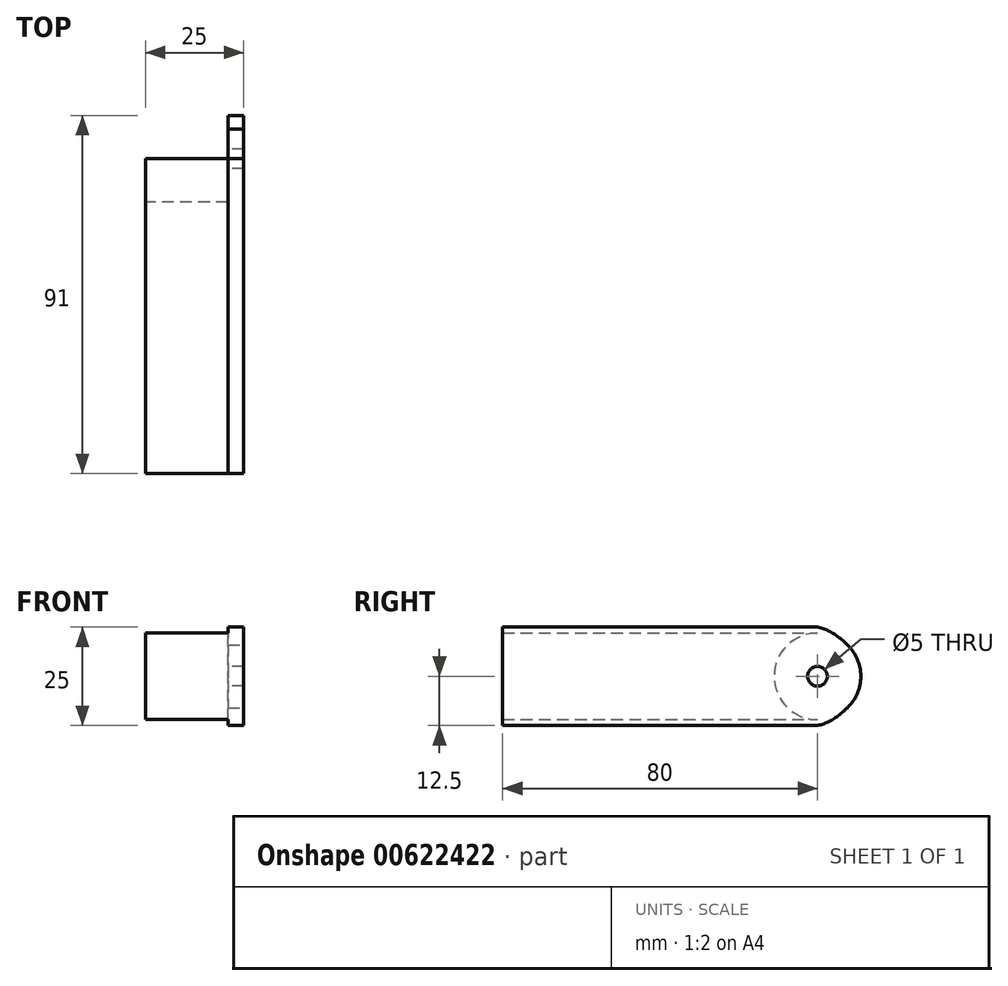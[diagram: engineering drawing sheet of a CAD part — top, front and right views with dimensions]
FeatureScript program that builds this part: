
annotation { "Feature Type Name" : "Feature", "Feature Type Description" : "" }
export const myFeature = defineFeature(function(context is Context, id is Id, definition is map)
    precondition{}
    {
        {
            var Q0;
            Q0=qCreatedBy(makeId("Front.planeOp"),FACE);
            var sketch = newSketch(context, id + "F0", { "sketchPlane" : qUnion([Q0])});
            skLineSegment(sketch, "E0.bottom", {"start": v(12.5, -12.5) * mm, "end": v(-12.5, -12.5) * mm});
            skLineSegment(sketch, "E0.top", {"start": v(12.5, 12.5) * mm, "end": v(-12.5, 12.5) * mm});
            skLineSegment(sketch, "E0.left", {"start": v(12.5, -12.5) * mm, "end": v(12.5, 12.5) * mm});
            skLineSegment(sketch, "E0.right", {"start": v(-12.5, -12.5) * mm, "end": v(-12.5, 12.5) * mm});
            skPoint(sketch, "E0.middle", {"position": v(0, 0) * mm});
            skSolve(sketch);
        }
        {
            var Q0;
            Q0 = qSketchRegion(id + "F0", true);
            extrude(context, id + "F1", {"entities" : qUnion([Q0]), "endBound" : BoundingType.SYMMETRIC, "depth" : 80 * mm, "offsetDistance" : 25 * mm});
        }
        {
            var Q0;
            Q0=makeQuery(id+"F1.opExtrude","SWEPT_FACE",FACE,{"disambiguationData":[OSD([sQuery(id+"F0.wireOp",EDGE,"E0.top")])]});
            var sketch = newSketch(context, id + "F2", { "sketchPlane" : qUnion([Q0])});
            skLineSegment(sketch, "E1.bottom", {"start": v(-12.5, 40) * mm, "end": v(8.5, 40) * mm});
            skLineSegment(sketch, "E1.top", {"start": v(-12.5, -40) * mm, "end": v(8.5, -40) * mm});
            skLineSegment(sketch, "E1.left", {"start": v(-12.5, 40) * mm, "end": v(-12.5, -40) * mm});
            skLineSegment(sketch, "E1.right", {"start": v(8.5, 40) * mm, "end": v(8.5, -40) * mm});
            skSolve(sketch);
        }
        {
            var Q0;
            Q0 = qSketchRegion(id + "F2", true);
            extrude(context, id + "F3", {"entities" : qUnion([Q0]), "operationType" : NewBodyOperationType.REMOVE, "oppositeDirection" : true, "depth" : 1.5 * mm, "offsetDistance" : 25 * mm});
        }
        {
            var Q0;
            Q0=makeQuery(id+"F1.opExtrude","SWEPT_FACE",FACE,{"disambiguationData":[OSD([sQuery(id+"F0.wireOp",EDGE,"E0.bottom")])]});
            var sketch = newSketch(context, id + "F4", { "sketchPlane" : qUnion([Q0])});
            skLineSegment(sketch, "E2.bottom", {"start": v(-12.5, 40) * mm, "end": v(8.5, 40) * mm});
            skLineSegment(sketch, "E2.top", {"start": v(-12.5, -40) * mm, "end": v(8.5, -40) * mm});
            skLineSegment(sketch, "E2.left", {"start": v(-12.5, 40) * mm, "end": v(-12.5, -40) * mm});
            skLineSegment(sketch, "E2.right", {"start": v(8.5, 40) * mm, "end": v(8.5, -40) * mm});
            skSolve(sketch);
        }
        {
            var Q0;
            Q0 = qSketchRegion(id + "F4", true);
            extrude(context, id + "F5", {"entities" : qUnion([Q0]), "operationType" : NewBodyOperationType.REMOVE, "oppositeDirection" : true, "depth" : 1.5 * mm, "offsetDistance" : 25 * mm});
        }
        {
            var Q0;
            Q0=makeQuery(id+"F1.opExtrude","SWEPT_FACE",FACE,{"disambiguationData":[OSD([sQuery(id+"F0.wireOp",EDGE,"E0.right")])]});
            var sketch = newSketch(context, id + "F6", { "sketchPlane" : qUnion([Q0])});
            skArc(sketch, "E3", {"start": v(-40, -11) * mm, "mid": v(-29, 0) * mm, "end": v(-40, 11) * mm});
            skLineSegment(sketch, "E4", {"start": v(-40, 11) * mm, "end": v(-40, -11) * mm});
            skSolve(sketch);
        }
        {
            var Q0;
            Q0 = qSketchRegion(id + "F6", true);
            extrude(context, id + "F7", {"entities" : qUnion([Q0]), "operationType" : NewBodyOperationType.REMOVE, "oppositeDirection" : true, "depth" : 21 * mm, "offsetDistance" : 25 * mm});
        }
        {
            var Q0;
            Q0=makeQuery(id+"F7.boolean.opBoolean","COPY",FACE,{"derivedFrom":makeQuery(id+"F7.opExtrude","CAP_FACE",FACE,{"disambiguationData":[OSD([sQuery(id+"F6.wireOp",EDGE,"E3"),sQuery(id+"F6.wireOp",EDGE,"E4")])],"isStart":false})});
            var sketch = newSketch(context, id + "F8", { "sketchPlane" : qUnion([Q0])});
            skLineSegment(sketch, "E5", {"start": v(-40, 11) * mm, "end": v(-40, -11) * mm});
            skArc(sketch, "E6", {"start": v(-40, 11) * mm, "mid": v(-51, 0) * mm, "end": v(-40, -11) * mm});
            skSolve(sketch);
        }
        {
            var Q0;
            Q0 = qSketchRegion(id + "F8", true);
            extrude(context, id + "F9", {"entities" : qUnion([Q0]), "operationType" : NewBodyOperationType.ADD, "oppositeDirection" : true, "depth" : 4 * mm, "offsetDistance" : 25 * mm});
        }
        {
            var Q0;
            Q0=makeQuery(id+"F9.boolean.opBoolean","MERGE",FACE,{"derivedFrom":[makeQuery(id+"F7.boolean.opBoolean","COPY",FACE,{"derivedFrom":makeQuery(id+"F7.opExtrude","CAP_FACE",FACE,{"disambiguationData":[OSD([sQuery(id+"F6.wireOp",EDGE,"E3"),sQuery(id+"F6.wireOp",EDGE,"E4")])],"isStart":false})}),makeQuery(id+"F9.opExtrude","CAP_FACE",FACE,{"disambiguationData":[OSD([sQuery(id+"F8.wireOp",EDGE,"E5"),sQuery(id+"F8.wireOp",EDGE,"E6")])],"isStart":true})]});
            var sketch = newSketch(context, id + "F10", { "sketchPlane" : qUnion([Q0])});
            skCircle(sketch, "E7", {"center": v(-40, 0) * mm, "radius": 2.5 * mm});
            skSolve(sketch);
        }
        {
            var Q0;
            Q0 = qSketchRegion(id + "F10", true);
            extrude(context, id + "F11", {"entities" : qUnion([Q0]), "operationType" : NewBodyOperationType.REMOVE, "endBound" : BoundingType.THROUGH_ALL, "oppositeDirection" : true, "depth" : 25 * mm, "offsetDistance" : 25 * mm});
        }
        {
            var Q0;
            Q0=makeQuery(id+"F9.boolean.opBoolean","MERGE",FACE,{"derivedFrom":[makeQuery(id+"F1.opExtrude","SWEPT_FACE",FACE,{"disambiguationData":[OSD([sQuery(id+"F0.wireOp",EDGE,"E0.left")])]}),makeQuery(id+"F9.opExtrude","CAP_FACE",FACE,{"disambiguationData":[OSD([sQuery(id+"F8.wireOp",EDGE,"E5"),sQuery(id+"F8.wireOp",EDGE,"E6")])],"isStart":false})]});
            var sketch = newSketch(context, id + "F12", { "sketchPlane" : qUnion([Q0])});
            skFitSpline(sketch, "E8", {"points": [v(40, 12.5) * mm, v(48.77, 6.64) * mm], "startDerivative": vector(14.46, -2.55) * mm, "endDerivative": vector(0.33, -0.42) * mm});
            skLineSegment(sketch, "E9", {"start": v(40, 12.5) * mm, "end": v(40, 11) * mm});
            skArc(sketch, "E10", {"start": v(48.77, 6.64) * mm, "mid": v(44.9, 9.85) * mm, "end": v(40, 11) * mm});
            skLineSegment(sketch, "E11.MirrorCS", {"start": v(40, -12.5) * mm, "end": v(40, -11) * mm});
            skFitSpline(sketch, "E12.MirrorCS", {"points": [v(40, -12.5) * mm, v(48.77, -6.64) * mm], "startDerivative": vector(14.46, 2.55) * mm, "endDerivative": vector(0.33, 0.42) * mm});
            skArc(sketch, "E13.MirrorCS", {"start": v(48.77, -6.64) * mm, "mid": v(44.9, -9.85) * mm, "end": v(40, -11) * mm});
            skSolve(sketch);
        }
        {
            var Q0;
            Q0 = qSketchRegion(id + "F12", true);
            extrude(context, id + "F13", {"entities" : qUnion([Q0]), "operationType" : NewBodyOperationType.ADD, "oppositeDirection" : true, "depth" : 4 * mm, "offsetDistance" : 25 * mm});
        }
    });
